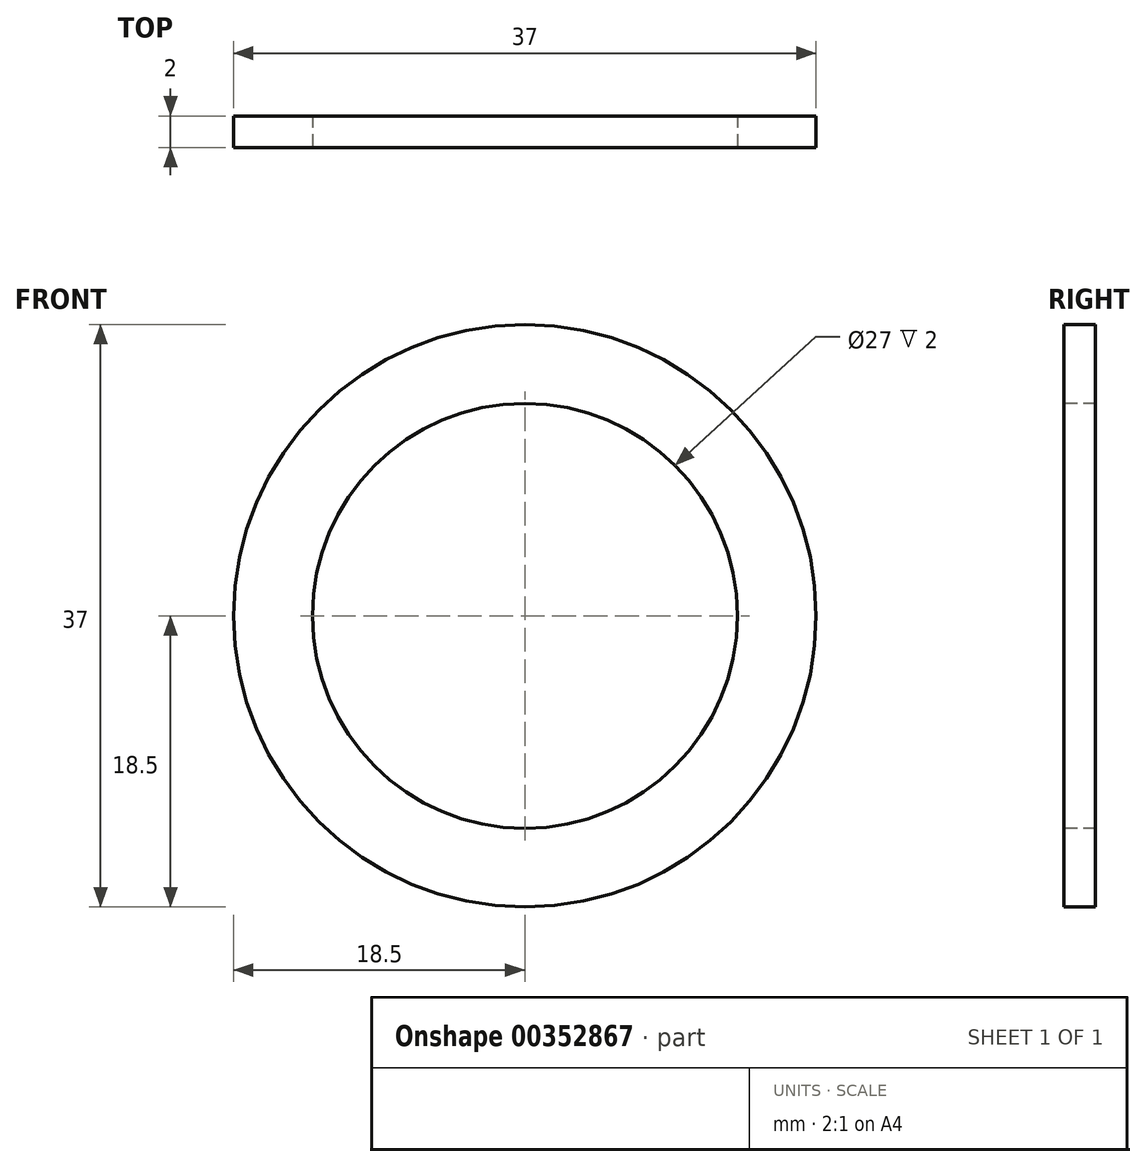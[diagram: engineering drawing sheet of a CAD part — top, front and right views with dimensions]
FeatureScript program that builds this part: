
annotation { "Feature Type Name" : "Feature", "Feature Type Description" : "" }
export const myFeature = defineFeature(function(context is Context, id is Id, definition is map)
    precondition{}
    {
        {
            var Q0;
            Q0=qCreatedBy(makeId("Front.planeOp"),FACE);
            var sketch = newSketch(context, id + "F0", { "sketchPlane" : qUnion([Q0])});
            skCircle(sketch, "E0", {"center": v(0, 0) * mm, "radius": 18.5 * mm});
            skCircle(sketch, "E1", {"center": v(0, 0) * mm, "radius": 13.5 * mm});
            skSolve(sketch);
        }
        {
            var Q0;
            Q0=makeQuery(id+"F0.imprint","IMPRINT",FACE,{"disambiguationData":[TD([[makeQuery(id+"F0.imprint","IMPRINT",EDGE,{"derivedFrom":sQuery(id+"F0.wireOp",EDGE,"E0")}),1.0]])]});
            extrude(context, id + "F1", {"entities" : qUnion([Q0]), "oppositeDirection" : true, "depth" : 2 * mm});
        }
    });
